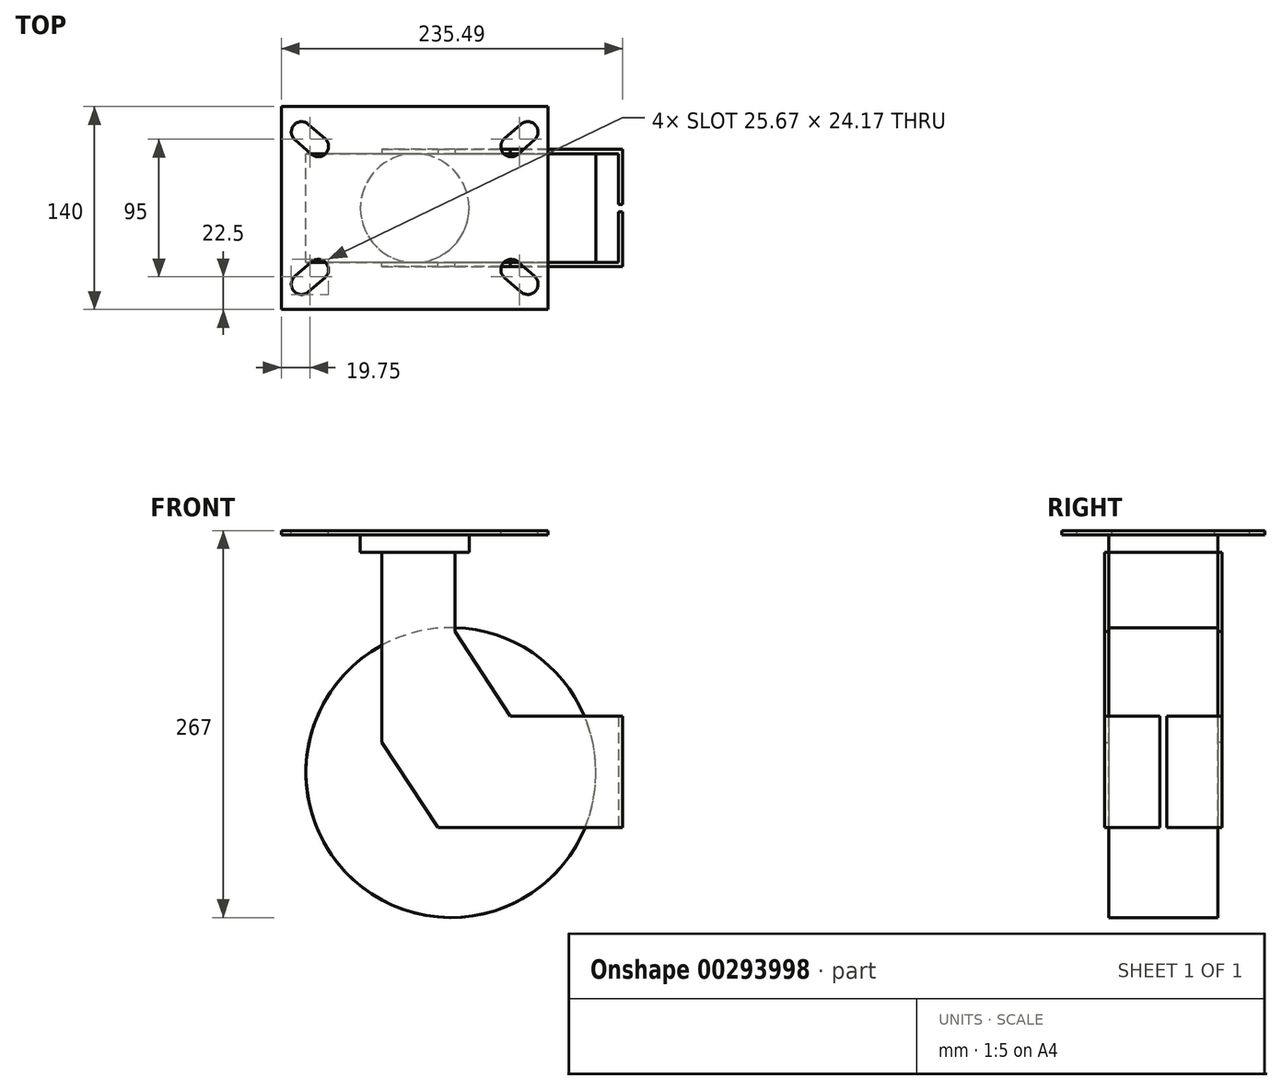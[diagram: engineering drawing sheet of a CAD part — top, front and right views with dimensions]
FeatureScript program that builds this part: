
annotation { "Feature Type Name" : "Feature", "Feature Type Description" : "" }
export const myFeature = defineFeature(function(context is Context, id is Id, definition is map)
    precondition{}
    {
        {
            var Q0;
            Q0=qCreatedBy(makeId("Top.planeOp"),FACE);
            var sketch = newSketch(context, id + "F0", { "sketchPlane" : qUnion([Q0])});
            skLineSegment(sketch, "E0.bottom", {"start": v(-92, 70) * mm, "end": v(92, 70) * mm});
            skLineSegment(sketch, "E0.top", {"start": v(-92, -70) * mm, "end": v(92, -70) * mm});
            skLineSegment(sketch, "E0.left", {"start": v(-92, 70) * mm, "end": v(-92, -70) * mm});
            skLineSegment(sketch, "E0.right", {"start": v(92, 70) * mm, "end": v(92, -70) * mm});
            skPoint(sketch, "E0.middle", {"position": v(0, 0) * mm});
            skPoint(sketch, "E1", {"position": v(-92, 0) * mm});
            skPoint(sketch, "E2", {"position": v(0, 70) * mm});
            skLineSegment(sketch, "E3.bottom", {"start": v(-66.5, 42.5) * mm, "end": v(66.5, 42.5) * mm, "construction": true});
            skLineSegment(sketch, "E3.top", {"start": v(-66.5, -42.5) * mm, "end": v(66.5, -42.5) * mm, "construction": true});
            skLineSegment(sketch, "E3.left", {"start": v(-66.5, 42.5) * mm, "end": v(-66.5, -42.5) * mm, "construction": true});
            skLineSegment(sketch, "E3.right", {"start": v(66.5, 42.5) * mm, "end": v(66.5, -42.5) * mm, "construction": true});
            skLineSegment(sketch, "E4.bottom", {"start": v(-78, 52.5) * mm, "end": v(78, 52.5) * mm, "construction": true});
            skLineSegment(sketch, "E4.top", {"start": v(-78, -52.5) * mm, "end": v(78, -52.5) * mm, "construction": true});
            skLineSegment(sketch, "E4.left", {"start": v(-78, 52.5) * mm, "end": v(-78, -52.5) * mm, "construction": true});
            skLineSegment(sketch, "E4.right", {"start": v(78, 52.5) * mm, "end": v(78, -52.5) * mm, "construction": true});
            skArc(sketch, "E5", {"start": v(-73.34, 57.86) * mm, "mid": v(-83.36, 57.16) * mm, "end": v(-82.66, 47.14) * mm});
            skArc(sketch, "E6", {"start": v(-71.16, 37.14) * mm, "mid": v(-61.14, 37.84) * mm, "end": v(-61.84, 47.86) * mm});
            skArc(sketch, "E7", {"start": v(82.66, 47.14) * mm, "mid": v(83.36, 57.16) * mm, "end": v(73.34, 57.86) * mm});
            skArc(sketch, "E8", {"start": v(61.84, 47.86) * mm, "mid": v(61.14, 37.84) * mm, "end": v(71.16, 37.14) * mm});
            skArc(sketch, "E9", {"start": v(71.16, -37.14) * mm, "mid": v(61.14, -37.84) * mm, "end": v(61.84, -47.86) * mm});
            skArc(sketch, "E10", {"start": v(73.34, -57.86) * mm, "mid": v(83.36, -57.16) * mm, "end": v(82.66, -47.14) * mm});
            skArc(sketch, "E11", {"start": v(-61.84, -47.86) * mm, "mid": v(-61.14, -37.84) * mm, "end": v(-71.16, -37.14) * mm});
            skArc(sketch, "E12", {"start": v(-82.66, -47.14) * mm, "mid": v(-83.36, -57.16) * mm, "end": v(-73.34, -57.86) * mm});
            skLineSegment(sketch, "E13", {"start": v(-73.34, 57.86) * mm, "end": v(-61.84, 47.86) * mm});
            skLineSegment(sketch, "E14", {"start": v(-82.66, 47.14) * mm, "end": v(-71.16, 37.14) * mm});
            skLineSegment(sketch, "E15", {"start": v(73.34, 57.86) * mm, "end": v(61.84, 47.86) * mm});
            skLineSegment(sketch, "E16", {"start": v(82.66, 47.14) * mm, "end": v(71.16, 37.14) * mm});
            skLineSegment(sketch, "E17", {"start": v(61.84, -47.86) * mm, "end": v(73.34, -57.86) * mm});
            skLineSegment(sketch, "E18", {"start": v(71.16, -37.14) * mm, "end": v(82.66, -47.14) * mm});
            skLineSegment(sketch, "E19", {"start": v(-61.84, -47.86) * mm, "end": v(-73.34, -57.86) * mm});
            skLineSegment(sketch, "E20", {"start": v(-71.16, -37.14) * mm, "end": v(-82.66, -47.14) * mm});
            skSolve(sketch);
        }
        {
            var Q0;
            Q0 = qSketchRegion(id + "F0", true);
            extrude(context, id + "F1", {"entities" : qUnion([Q0]), "oppositeDirection" : true, "depth" : 3 * mm});
        }
        {
            var Q0;
            Q0=makeQuery(id+"F1.opExtrude","CAP_FACE",FACE,{"disambiguationData":[OSD([sQuery(id+"F0.wireOp",EDGE,"E0.bottom"),sQuery(id+"F0.wireOp",EDGE,"E0.top"),sQuery(id+"F0.wireOp",EDGE,"E0.left"),sQuery(id+"F0.wireOp",EDGE,"E0.right"),sQuery(id+"F0.wireOp",EDGE,"E5"),sQuery(id+"F0.wireOp",EDGE,"E6"),sQuery(id+"F0.wireOp",EDGE,"E7"),sQuery(id+"F0.wireOp",EDGE,"E8"),sQuery(id+"F0.wireOp",EDGE,"E9"),sQuery(id+"F0.wireOp",EDGE,"E10"),sQuery(id+"F0.wireOp",EDGE,"E11"),sQuery(id+"F0.wireOp",EDGE,"E12"),sQuery(id+"F0.wireOp",EDGE,"E13"),sQuery(id+"F0.wireOp",EDGE,"E14"),sQuery(id+"F0.wireOp",EDGE,"E15"),sQuery(id+"F0.wireOp",EDGE,"E16"),sQuery(id+"F0.wireOp",EDGE,"E17"),sQuery(id+"F0.wireOp",EDGE,"E18"),sQuery(id+"F0.wireOp",EDGE,"E19"),sQuery(id+"F0.wireOp",EDGE,"E20")])],"isStart":false});
            var sketch = newSketch(context, id + "F2", { "sketchPlane" : qUnion([Q0])});
            skCircle(sketch, "E21", {"center": v(0, 0) * mm, "radius": 37.5 * mm});
            skSolve(sketch);
        }
        {
            var Q0;
            Q0 = qSketchRegion(id + "F2", true);
            extrude(context, id + "F3", {"entities" : qUnion([Q0]), "operationType" : NewBodyOperationType.ADD, "depth" : 12 * mm});
        }
        {
            var Q0;
            Q0=qCreatedBy(makeId("Top.planeOp"),FACE);
            cPlane(context, id + "F4", {"entities" : qUnion([Q0]), "cplaneType" : CPlaneType.OFFSET, "offset" : 167 * mm, "oppositeDirection" : true, "width" : 150 * mm, "height" : 150 * mm});
        }
        {
            var Q0;
            Q0=qCreatedBy(makeId("Right.planeOp"),FACE);
            cPlane(context, id + "F5", {"entities" : qUnion([Q0]), "cplaneType" : CPlaneType.OFFSET, "offset" : 25 * mm, "width" : 150 * mm, "height" : 150 * mm});
        }
        {
            var Q0;
            Q0=qCreatedBy(makeId("Front.planeOp"),FACE);
            var sketch = newSketch(context, id + "F6", { "sketchPlane" : qUnion([Q0])});
            skCircle(sketch, "E22", {"center": v(25, -167) * mm, "radius": 100 * mm});
            skSolve(sketch);
        }
        {
            var Q0;
            Q0 = qSketchRegion(id + "F6", true);
            extrude(context, id + "F7", {"entities" : qUnion([Q0]), "endBound" : BoundingType.SYMMETRIC, "depth" : 75 * mm});
        }
        {
            var Q0;
            Q0=makeQuery(id+"F7.opExtrude","CAP_FACE",FACE,{"disambiguationData":[OSD([sQuery(id+"F6.wireOp",EDGE,"E22")])],"isStart":false});
            var sketch = newSketch(context, id + "F8", { "sketchPlane" : qUnion([Q0])});
            skLineSegment(sketch, "E23.0", {"start": v(37.5, -15) * mm, "end": v(-37.5, -15) * mm, "construction": true});
            skCircle(sketch, "E24.0", {"center": v(25, -167) * mm, "radius": 100 * mm, "construction": true});
            skLineSegment(sketch, "E25", {"start": v(-22.7, -15) * mm, "end": v(-22.7, -146.05) * mm});
            skLineSegment(sketch, "E26", {"start": v(-22.7, -146.05) * mm, "end": v(16.03, -204.78) * mm});
            skLineSegment(sketch, "E27", {"start": v(16.03, -204.78) * mm, "end": v(143.5, -204.78) * mm});
            skLineSegment(sketch, "E28", {"start": v(143.5, -204.78) * mm, "end": v(143.5, -127.93) * mm});
            skLineSegment(sketch, "E29", {"start": v(143.5, -127.93) * mm, "end": v(66.02, -127.93) * mm});
            skLineSegment(sketch, "E30", {"start": v(66.02, -127.93) * mm, "end": v(27.67, -69.79) * mm});
            skLineSegment(sketch, "E31", {"start": v(27.67, -69.79) * mm, "end": v(27.67, -15) * mm});
            skLineSegment(sketch, "E32", {"start": v(27.67, -15) * mm, "end": v(-22.7, -15) * mm});
            skSolve(sketch);
        }
        {
            var Q0;
            Q0 = qSketchRegion(id + "F8", true);
            extrude(context, id + "F9", {"entities" : qUnion([Q0]), "operationType" : NewBodyOperationType.ADD, "depth" : 3 * mm});
        }
        {
            var Q0;
            {var subQ0=sQuery(id+"F8.wireOp",EDGE,"E28");var subQ1=sQuery(id+"F8.wireOp",EDGE,"E27");var subQ3=sQuery(id+"F8.wireOp",EDGE,"E29");Q0=makeQuery(id+"F9.boolean.opBoolean","SPLIT",FACE,{"disambiguationData":[TD([makeQuery(id+"F9.opExtrude","SWEPT_FACE",FACE,{"disambiguationData":[OSD([subQ1])]})])],"derivedFrom":makeQuery(id+"F9.opExtrude","CAP_FACE",FACE,{"disambiguationData":[OSD([sQuery(id+"F8.wireOp",EDGE,"E25"),sQuery(id+"F8.wireOp",EDGE,"E26"),subQ1,subQ0,subQ3,sQuery(id+"F8.wireOp",EDGE,"E30"),sQuery(id+"F8.wireOp",EDGE,"E31"),sQuery(id+"F8.wireOp",EDGE,"E32")])],"isStart":true})});}
            var sketch = newSketch(context, id + "F10", { "sketchPlane" : qUnion([Q0])});
            skLineSegment(sketch, "E33.0", {"start": v(-143.5, -204.78) * mm, "end": v(-143.5, -127.93) * mm});
            skLineSegment(sketch, "E34", {"start": v(-143.5, -127.93) * mm, "end": v(-140.5, -127.93) * mm});
            skLineSegment(sketch, "E35", {"start": v(-140.5, -127.93) * mm, "end": v(-140.5, -204.78) * mm});
            skLineSegment(sketch, "E36", {"start": v(-140.5, -204.78) * mm, "end": v(-143.5, -204.78) * mm});
            skSolve(sketch);
        }
        {
            var Q0;
            Q0 = qSketchRegion(id + "F10", true);
            extrude(context, id + "F11", {"entities" : qUnion([Q0]), "operationType" : NewBodyOperationType.ADD, "depth" : 35 * mm});
        }
        {
            var Q0;
            Q0=makeQuery(id+"F7.opExtrude","SWEPT_BODY",BODY,{"disambiguationData":[OSD([sQuery(id+"F6.wireOp",EDGE,"E22")])]});
            var Q1;
            Q1=qCreatedBy(makeId("Front.planeOp"),FACE);
            mirror(context, id + "F12", {"operationType" : NewBodyOperationType.ADD, "entities" : qUnion([Q0]), "mirrorPlane" : qUnion([Q1])});
        }
    });
